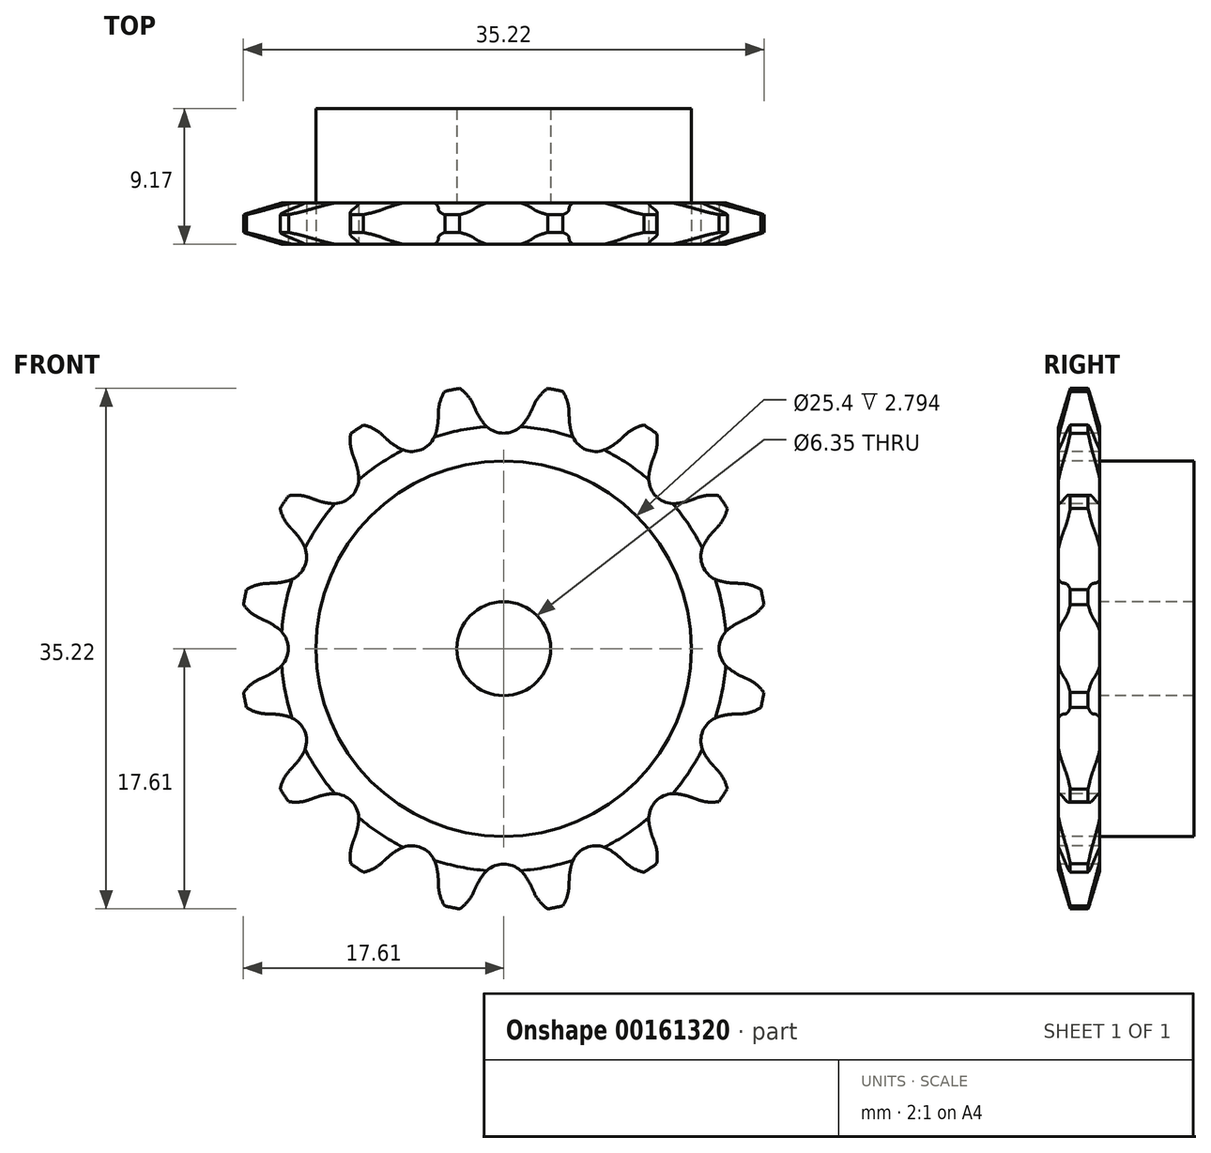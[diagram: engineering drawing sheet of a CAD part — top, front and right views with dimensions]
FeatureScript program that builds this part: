
annotation { "Feature Type Name" : "Feature", "Feature Type Description" : "" }
export const myFeature = defineFeature(function(context is Context, id is Id, definition is map)
    precondition{}
    {
        {
            var Q0;
            Q0=qCreatedBy(makeId("Right.planeOp"),FACE);
            var sketch = newSketch(context, id + "F0", { "sketchPlane" : qUnion([Q0])});
            skLineSegment(sketch, "E0", {"start": v(0, 0) * mm, "end": v(11.72, 0) * mm, "construction": true});
            skLineSegment(sketch, "E1.bottom", {"start": v(0, 3.18) * mm, "end": v(2.8, 3.18) * mm});
            skLineSegment(sketch, "E1.top", {"start": v(0, 17.86) * mm, "end": v(2.8, 17.86) * mm});
            skLineSegment(sketch, "E1.left", {"start": v(0, 3.18) * mm, "end": v(0, 17.86) * mm});
            skLineSegment(sketch, "E1.right", {"start": v(2.8, 3.18) * mm, "end": v(2.8, 17.86) * mm});
            skLineSegment(sketch, "E2.bottom", {"start": v(0, 3.18) * mm, "end": v(9.17, 3.18) * mm});
            skLineSegment(sketch, "E2.top", {"start": v(0, 12.7) * mm, "end": v(9.17, 12.7) * mm});
            skLineSegment(sketch, "E2.left", {"start": v(0, 3.18) * mm, "end": v(0, 12.7) * mm});
            skLineSegment(sketch, "E2.right", {"start": v(9.17, 3.18) * mm, "end": v(9.17, 12.7) * mm});
            skLineSegment(sketch, "E3.MirrorCS", {"start": v(0, -17.86) * mm, "end": v(2.8, -17.86) * mm});
            skLineSegment(sketch, "E4.MirrorCS", {"start": v(0, -3.18) * mm, "end": v(2.8, -3.18) * mm});
            skLineSegment(sketch, "E5.MirrorCS", {"start": v(9.17, -3.18) * mm, "end": v(9.17, -12.7) * mm});
            skLineSegment(sketch, "E6.MirrorCS", {"start": v(0, -3.18) * mm, "end": v(0, -17.86) * mm});
            skLineSegment(sketch, "E7.MirrorCS", {"start": v(2.8, -3.18) * mm, "end": v(2.8, -17.86) * mm});
            skLineSegment(sketch, "E8.MirrorCS", {"start": v(0, -3.18) * mm, "end": v(9.17, -3.18) * mm});
            skLineSegment(sketch, "E9.MirrorCS", {"start": v(0, -12.7) * mm, "end": v(9.17, -12.7) * mm});
            skLineSegment(sketch, "E10.MirrorCS", {"start": v(0, -3.18) * mm, "end": v(0, -12.7) * mm});
            skLineSegment(sketch, "E11.bottom", {"start": v(9.17, 3.18) * mm, "end": v(11.96, 3.18) * mm});
            skLineSegment(sketch, "E11.top", {"start": v(9.17, 17.86) * mm, "end": v(11.96, 17.86) * mm});
            skLineSegment(sketch, "E11.left", {"start": v(9.17, 3.18) * mm, "end": v(9.17, 17.86) * mm});
            skLineSegment(sketch, "E11.right", {"start": v(11.96, 3.18) * mm, "end": v(11.96, 17.86) * mm});
            skLineSegment(sketch, "E12.MirrorCS", {"start": v(9.17, -3.18) * mm, "end": v(9.17, -17.86) * mm});
            skLineSegment(sketch, "E13.MirrorCS", {"start": v(9.17, -17.86) * mm, "end": v(11.96, -17.86) * mm});
            skLineSegment(sketch, "E14.MirrorCS", {"start": v(11.96, -3.18) * mm, "end": v(11.96, -17.86) * mm});
            skLineSegment(sketch, "E15.MirrorCS", {"start": v(9.17, -3.18) * mm, "end": v(11.96, -3.18) * mm});
            skSolve(sketch);
        }
        {
            var Q0;
            {var subQ5=sQuery(id+"F0.wireOp",EDGE,"E2.right");Q0=makeQuery(id+"F0.imprint","IMPRINT",FACE,{"disambiguationData":[TD([[makeQuery(id+"F0.imprint","IMPRINT",EDGE,{"derivedFrom":subQ5}),1.0]])]});}
            var Q1;
            {var subQ5=sQuery(id+"F0.wireOp",EDGE,"E2.left");Q1=makeQuery(id+"F0.imprint","IMPRINT",FACE,{"disambiguationData":[TD([[makeQuery(id+"F0.imprint","IMPRINT",EDGE,{"derivedFrom":subQ5}),-1.0]])]});}
            var Q2;
            {var subQ0=sQuery(id+"F0.wireOp",EDGE,"E1.top");Q2=makeQuery(id+"F0.imprint","IMPRINT",FACE,{"disambiguationData":[TD([[makeQuery(id+"F0.imprint","IMPRINT",EDGE,{"derivedFrom":subQ0}),-1.0]])]});}
            var Q3;
            Q3=sQuery(id+"F0.wireOp",EDGE,"E0");
            revolve(context, id + "F1", {"entities" : qUnion([Q0, Q1, Q2]), "axis" : qUnion([Q3]), "revolveType" : RevolveType.FULL});
        }
        {
            var Q0;
            Q0=makeQuery(id+"F1.opRevolve","SWEPT_EDGE",EDGE,{"disambiguationData":[OSD([sQuery(id+"F0.wireOp",EDGE,"E1.top"),sQuery(id+"F0.wireOp",EDGE,"E1.left")])]});
            var Q1;
            Q1=makeQuery(id+"F1.opRevolve","SWEPT_EDGE",EDGE,{"disambiguationData":[OSD([sQuery(id+"F0.wireOp",EDGE,"E1.top"),sQuery(id+"F0.wireOp",EDGE,"E1.right")])]});
            chamfer(context, id + "F2", {"entities" : qUnion([Q0, Q1]), "chamferType" : ChamferType.TWO_OFFSETS, "width1" : 2.8 * mm, "oppositeDirection" : false, "width2" : 0.8 * mm, "tangentPropagation" : true});
        }
        {
            var Q0;
            Q0=makeQuery(id+"F1.opRevolve","SWEPT_FACE",FACE,{"disambiguationData":[OSD([sQuery(id+"F0.wireOp",EDGE,"E1.left"),sQuery(id+"F0.wireOp",EDGE,"E2.left")])]});
            var sketch = newSketch(context, id + "F3", { "sketchPlane" : qUnion([Q0])});
            skCircle(sketch, "E16", {"center": v(0, 0) * mm, "radius": 16.28 * mm, "construction": true});
            skLineSegment(sketch, "E17", {"start": v(0, 0) * mm, "end": v(0, 16.28) * mm, "construction": true});
            skLineSegment(sketch, "E18", {"start": v(0, 16.28) * mm, "end": v(74.18, 16.28) * mm, "construction": true});
            skLineSegment(sketch, "E19", {"start": v(0, 16.28) * mm, "end": v(2.06, 17.93) * mm, "construction": true});
            skLineSegment(sketch, "E20", {"start": v(2.06, 17.93) * mm, "end": v(-1.9, 16.15) * mm, "construction": true});
            skLineSegment(sketch, "E21", {"start": v(-1.9, 16.15) * mm, "end": v(-2.05, 16.5) * mm});
            skLineSegment(sketch, "E22", {"start": v(0, 0) * mm, "end": v(-3.56, 17.92) * mm, "construction": true});
            skArc(sketch, "E23", {"start": v(-3.56, 17.92) * mm, "mid": v(-6.4, 13.4) * mm, "end": v(-2.05, 16.5) * mm, "construction": true});
            skArc(sketch, "E24", {"start": v(-2.05, 16.5) * mm, "mid": v(-2.67, 17.35) * mm, "end": v(-3.56, 17.92) * mm});
            skLineSegment(sketch, "E25", {"start": v(7.6, -4.93) * mm, "end": v(-1.9, 16.16) * mm, "construction": true});
            skArc(sketch, "E26", {"start": v(-1.9, 16.15) * mm, "mid": v(-1.64, 15.66) * mm, "end": v(-1.32, 15.21) * mm});
            skArc(sketch, "E27", {"start": v(-1.32, 15.21) * mm, "mid": v(5.76, 20.2) * mm, "end": v(-1.9, 16.15) * mm, "construction": true});
            skArc(sketch, "E28.0.MirrorCS", {"start": v(1.9, 16.15) * mm, "mid": v(1.64, 15.66) * mm, "end": v(1.32, 15.21) * mm});
            skLineSegment(sketch, "E29.0.MirrorCS", {"start": v(1.9, 16.15) * mm, "end": v(2.05, 16.5) * mm});
            skArc(sketch, "E30.0.MirrorCS", {"start": v(2.05, 16.5) * mm, "mid": v(2.67, 17.35) * mm, "end": v(3.56, 17.92) * mm});
            skArc(sketch, "E31", {"start": v(-1.32, 15.21) * mm, "mid": v(0, 14.58) * mm, "end": v(1.32, 15.21) * mm});
            skArc(sketch, "E32", {"start": v(1.32, 15.21) * mm, "mid": v(0, 17.97) * mm, "end": v(-1.32, 15.21) * mm, "construction": true});
            skArc(sketch, "E33.1.0", {"start": v(-7.93, 14.2) * mm, "mid": v(-7.5, 13.84) * mm, "end": v(-7.04, 13.55) * mm});
            skArc(sketch, "E33.1.1", {"start": v(-8.2, 14.45) * mm, "mid": v(-9.1, 15.01) * mm, "end": v(-10.15, 15.19) * mm});
            skLineSegment(sketch, "E33.1.2", {"start": v(-7.93, 14.2) * mm, "end": v(-8.2, 14.45) * mm});
            skArc(sketch, "E33.1.3", {"start": v(-7.04, 13.55) * mm, "mid": v(-5.58, 13.47) * mm, "end": v(-4.6, 14.56) * mm});
            skArc(sketch, "E33.1.4", {"start": v(-4.43, 15.64) * mm, "mid": v(-4.48, 15.1) * mm, "end": v(-4.6, 14.56) * mm});
            skArc(sketch, "E33.1.5", {"start": v(-4.42, 16.02) * mm, "mid": v(-4.18, 17.05) * mm, "end": v(-3.56, 17.92) * mm});
            skLineSegment(sketch, "E33.1.6", {"start": v(-4.43, 15.64) * mm, "end": v(-4.42, 16.02) * mm});
            skArc(sketch, "E33.2.0", {"start": v(-12.76, 10.08) * mm, "mid": v(-12.23, 9.91) * mm, "end": v(-11.7, 9.82) * mm});
            skArc(sketch, "E33.2.1", {"start": v(-13.11, 10.21) * mm, "mid": v(-14.16, 10.39) * mm, "end": v(-15.19, 10.15) * mm});
            skLineSegment(sketch, "E33.2.2", {"start": v(-12.76, 10.08) * mm, "end": v(-13.11, 10.21) * mm});
            skArc(sketch, "E33.2.3", {"start": v(-11.7, 9.82) * mm, "mid": v(-10.3, 10.3) * mm, "end": v(-9.82, 11.7) * mm});
            skArc(sketch, "E33.2.4", {"start": v(-10.08, 12.76) * mm, "mid": v(-9.91, 12.23) * mm, "end": v(-9.82, 11.7) * mm});
            skArc(sketch, "E33.2.5", {"start": v(-10.21, 13.11) * mm, "mid": v(-10.39, 14.16) * mm, "end": v(-10.15, 15.19) * mm});
            skLineSegment(sketch, "E33.2.6", {"start": v(-10.08, 12.76) * mm, "end": v(-10.21, 13.11) * mm});
            skArc(sketch, "E33.3.0", {"start": v(-15.64, 4.43) * mm, "mid": v(-15.1, 4.48) * mm, "end": v(-14.56, 4.6) * mm});
            skArc(sketch, "E33.3.1", {"start": v(-16.02, 4.42) * mm, "mid": v(-17.05, 4.18) * mm, "end": v(-17.92, 3.56) * mm});
            skLineSegment(sketch, "E33.3.2", {"start": v(-15.64, 4.43) * mm, "end": v(-16.02, 4.42) * mm});
            skArc(sketch, "E33.3.3", {"start": v(-14.56, 4.6) * mm, "mid": v(-13.47, 5.58) * mm, "end": v(-13.55, 7.04) * mm});
            skArc(sketch, "E33.3.4", {"start": v(-14.2, 7.93) * mm, "mid": v(-13.84, 7.5) * mm, "end": v(-13.55, 7.04) * mm});
            skArc(sketch, "E33.3.5", {"start": v(-14.45, 8.2) * mm, "mid": v(-15.01, 9.1) * mm, "end": v(-15.19, 10.15) * mm});
            skLineSegment(sketch, "E33.3.6", {"start": v(-14.2, 7.93) * mm, "end": v(-14.45, 8.2) * mm});
            skArc(sketch, "E33.4.0", {"start": v(-16.15, -1.9) * mm, "mid": v(-15.66, -1.64) * mm, "end": v(-15.21, -1.32) * mm});
            skArc(sketch, "E33.4.1", {"start": v(-16.5, -2.05) * mm, "mid": v(-17.35, -2.67) * mm, "end": v(-17.92, -3.56) * mm});
            skLineSegment(sketch, "E33.4.2", {"start": v(-16.15, -1.9) * mm, "end": v(-16.5, -2.05) * mm});
            skArc(sketch, "E33.4.3", {"start": v(-15.21, -1.32) * mm, "mid": v(-14.58, 0) * mm, "end": v(-15.21, 1.32) * mm});
            skArc(sketch, "E33.4.4", {"start": v(-16.15, 1.9) * mm, "mid": v(-15.66, 1.64) * mm, "end": v(-15.21, 1.32) * mm});
            skArc(sketch, "E33.4.5", {"start": v(-16.5, 2.05) * mm, "mid": v(-17.35, 2.67) * mm, "end": v(-17.92, 3.56) * mm});
            skLineSegment(sketch, "E33.4.6", {"start": v(-16.15, 1.9) * mm, "end": v(-16.5, 2.05) * mm});
            skArc(sketch, "E33.5.0", {"start": v(-14.2, -7.93) * mm, "mid": v(-13.84, -7.5) * mm, "end": v(-13.55, -7.04) * mm});
            skArc(sketch, "E33.5.1", {"start": v(-14.45, -8.2) * mm, "mid": v(-15.01, -9.1) * mm, "end": v(-15.19, -10.15) * mm});
            skLineSegment(sketch, "E33.5.2", {"start": v(-14.2, -7.93) * mm, "end": v(-14.45, -8.2) * mm});
            skArc(sketch, "E33.5.3", {"start": v(-13.55, -7.04) * mm, "mid": v(-13.47, -5.58) * mm, "end": v(-14.56, -4.6) * mm});
            skArc(sketch, "E33.5.4", {"start": v(-15.64, -4.43) * mm, "mid": v(-15.1, -4.48) * mm, "end": v(-14.56, -4.6) * mm});
            skArc(sketch, "E33.5.5", {"start": v(-16.02, -4.42) * mm, "mid": v(-17.05, -4.18) * mm, "end": v(-17.92, -3.56) * mm});
            skLineSegment(sketch, "E33.5.6", {"start": v(-15.64, -4.43) * mm, "end": v(-16.02, -4.42) * mm});
            skArc(sketch, "E33.6.0", {"start": v(-10.08, -12.76) * mm, "mid": v(-9.91, -12.23) * mm, "end": v(-9.82, -11.7) * mm});
            skArc(sketch, "E33.6.1", {"start": v(-10.21, -13.11) * mm, "mid": v(-10.39, -14.16) * mm, "end": v(-10.15, -15.19) * mm});
            skLineSegment(sketch, "E33.6.2", {"start": v(-10.08, -12.76) * mm, "end": v(-10.21, -13.11) * mm});
            skArc(sketch, "E33.6.3", {"start": v(-9.82, -11.7) * mm, "mid": v(-10.3, -10.3) * mm, "end": v(-11.7, -9.82) * mm});
            skArc(sketch, "E33.6.4", {"start": v(-12.76, -10.08) * mm, "mid": v(-12.23, -9.91) * mm, "end": v(-11.7, -9.82) * mm});
            skArc(sketch, "E33.6.5", {"start": v(-13.11, -10.21) * mm, "mid": v(-14.16, -10.39) * mm, "end": v(-15.19, -10.15) * mm});
            skLineSegment(sketch, "E33.6.6", {"start": v(-12.76, -10.08) * mm, "end": v(-13.11, -10.21) * mm});
            skArc(sketch, "E33.7.0", {"start": v(-4.43, -15.64) * mm, "mid": v(-4.48, -15.1) * mm, "end": v(-4.6, -14.56) * mm});
            skArc(sketch, "E33.7.1", {"start": v(-4.42, -16.02) * mm, "mid": v(-4.18, -17.05) * mm, "end": v(-3.56, -17.92) * mm});
            skLineSegment(sketch, "E33.7.2", {"start": v(-4.43, -15.64) * mm, "end": v(-4.42, -16.02) * mm});
            skArc(sketch, "E33.7.3", {"start": v(-4.6, -14.56) * mm, "mid": v(-5.58, -13.47) * mm, "end": v(-7.04, -13.55) * mm});
            skArc(sketch, "E33.7.4", {"start": v(-7.93, -14.2) * mm, "mid": v(-7.5, -13.84) * mm, "end": v(-7.04, -13.55) * mm});
            skArc(sketch, "E33.7.5", {"start": v(-8.2, -14.45) * mm, "mid": v(-9.1, -15.01) * mm, "end": v(-10.15, -15.19) * mm});
            skLineSegment(sketch, "E33.7.6", {"start": v(-7.93, -14.2) * mm, "end": v(-8.2, -14.45) * mm});
            skArc(sketch, "E33.8.0", {"start": v(1.9, -16.15) * mm, "mid": v(1.64, -15.66) * mm, "end": v(1.32, -15.21) * mm});
            skArc(sketch, "E33.8.1", {"start": v(2.05, -16.5) * mm, "mid": v(2.67, -17.35) * mm, "end": v(3.56, -17.92) * mm});
            skLineSegment(sketch, "E33.8.2", {"start": v(1.9, -16.15) * mm, "end": v(2.05, -16.5) * mm});
            skArc(sketch, "E33.8.3", {"start": v(1.32, -15.21) * mm, "mid": v(0, -14.58) * mm, "end": v(-1.32, -15.21) * mm});
            skArc(sketch, "E33.8.4", {"start": v(-1.9, -16.15) * mm, "mid": v(-1.64, -15.66) * mm, "end": v(-1.32, -15.21) * mm});
            skArc(sketch, "E33.8.5", {"start": v(-2.05, -16.5) * mm, "mid": v(-2.67, -17.35) * mm, "end": v(-3.56, -17.92) * mm});
            skLineSegment(sketch, "E33.8.6", {"start": v(-1.9, -16.15) * mm, "end": v(-2.05, -16.5) * mm});
            skArc(sketch, "E33.9.0", {"start": v(7.93, -14.2) * mm, "mid": v(7.5, -13.84) * mm, "end": v(7.04, -13.55) * mm});
            skArc(sketch, "E33.9.1", {"start": v(8.2, -14.45) * mm, "mid": v(9.1, -15.01) * mm, "end": v(10.15, -15.19) * mm});
            skLineSegment(sketch, "E33.9.2", {"start": v(7.93, -14.2) * mm, "end": v(8.2, -14.45) * mm});
            skArc(sketch, "E33.9.3", {"start": v(7.04, -13.55) * mm, "mid": v(5.58, -13.47) * mm, "end": v(4.6, -14.56) * mm});
            skArc(sketch, "E33.9.4", {"start": v(4.43, -15.64) * mm, "mid": v(4.48, -15.1) * mm, "end": v(4.6, -14.56) * mm});
            skArc(sketch, "E33.9.5", {"start": v(4.42, -16.02) * mm, "mid": v(4.18, -17.05) * mm, "end": v(3.56, -17.92) * mm});
            skLineSegment(sketch, "E33.9.6", {"start": v(4.43, -15.64) * mm, "end": v(4.42, -16.02) * mm});
            skArc(sketch, "E33.10.0", {"start": v(12.76, -10.08) * mm, "mid": v(12.23, -9.91) * mm, "end": v(11.7, -9.82) * mm});
            skArc(sketch, "E33.10.1", {"start": v(13.11, -10.21) * mm, "mid": v(14.16, -10.39) * mm, "end": v(15.19, -10.15) * mm});
            skLineSegment(sketch, "E33.10.2", {"start": v(12.76, -10.08) * mm, "end": v(13.11, -10.21) * mm});
            skArc(sketch, "E33.10.3", {"start": v(11.7, -9.82) * mm, "mid": v(10.3, -10.3) * mm, "end": v(9.82, -11.7) * mm});
            skArc(sketch, "E33.10.4", {"start": v(10.08, -12.76) * mm, "mid": v(9.91, -12.23) * mm, "end": v(9.82, -11.7) * mm});
            skArc(sketch, "E33.10.5", {"start": v(10.21, -13.11) * mm, "mid": v(10.39, -14.16) * mm, "end": v(10.15, -15.19) * mm});
            skLineSegment(sketch, "E33.10.6", {"start": v(10.08, -12.76) * mm, "end": v(10.21, -13.11) * mm});
            skArc(sketch, "E33.11.0", {"start": v(15.64, -4.43) * mm, "mid": v(15.1, -4.48) * mm, "end": v(14.56, -4.6) * mm});
            skArc(sketch, "E33.11.1", {"start": v(16.02, -4.42) * mm, "mid": v(17.05, -4.18) * mm, "end": v(17.92, -3.56) * mm});
            skLineSegment(sketch, "E33.11.2", {"start": v(15.64, -4.43) * mm, "end": v(16.02, -4.42) * mm});
            skArc(sketch, "E33.11.3", {"start": v(14.56, -4.6) * mm, "mid": v(13.47, -5.58) * mm, "end": v(13.55, -7.04) * mm});
            skArc(sketch, "E33.11.4", {"start": v(14.2, -7.93) * mm, "mid": v(13.84, -7.5) * mm, "end": v(13.55, -7.04) * mm});
            skArc(sketch, "E33.11.5", {"start": v(14.45, -8.2) * mm, "mid": v(15.01, -9.1) * mm, "end": v(15.19, -10.15) * mm});
            skLineSegment(sketch, "E33.11.6", {"start": v(14.2, -7.93) * mm, "end": v(14.45, -8.2) * mm});
            skArc(sketch, "E33.12.0", {"start": v(16.15, 1.9) * mm, "mid": v(15.66, 1.64) * mm, "end": v(15.21, 1.32) * mm});
            skArc(sketch, "E33.12.1", {"start": v(16.5, 2.05) * mm, "mid": v(17.35, 2.67) * mm, "end": v(17.92, 3.56) * mm});
            skLineSegment(sketch, "E33.12.2", {"start": v(16.15, 1.9) * mm, "end": v(16.5, 2.05) * mm});
            skArc(sketch, "E33.12.3", {"start": v(15.21, 1.32) * mm, "mid": v(14.58, 0) * mm, "end": v(15.21, -1.32) * mm});
            skArc(sketch, "E33.12.4", {"start": v(16.15, -1.9) * mm, "mid": v(15.66, -1.64) * mm, "end": v(15.21, -1.32) * mm});
            skArc(sketch, "E33.12.5", {"start": v(16.5, -2.05) * mm, "mid": v(17.35, -2.67) * mm, "end": v(17.92, -3.56) * mm});
            skLineSegment(sketch, "E33.12.6", {"start": v(16.15, -1.9) * mm, "end": v(16.5, -2.05) * mm});
            skArc(sketch, "E33.13.0", {"start": v(14.2, 7.93) * mm, "mid": v(13.84, 7.5) * mm, "end": v(13.55, 7.04) * mm});
            skArc(sketch, "E33.13.1", {"start": v(14.45, 8.2) * mm, "mid": v(15.01, 9.1) * mm, "end": v(15.19, 10.15) * mm});
            skLineSegment(sketch, "E33.13.2", {"start": v(14.2, 7.93) * mm, "end": v(14.45, 8.2) * mm});
            skArc(sketch, "E33.13.3", {"start": v(13.55, 7.04) * mm, "mid": v(13.47, 5.58) * mm, "end": v(14.56, 4.6) * mm});
            skArc(sketch, "E33.13.4", {"start": v(15.64, 4.43) * mm, "mid": v(15.1, 4.48) * mm, "end": v(14.56, 4.6) * mm});
            skArc(sketch, "E33.13.5", {"start": v(16.02, 4.42) * mm, "mid": v(17.05, 4.18) * mm, "end": v(17.92, 3.56) * mm});
            skLineSegment(sketch, "E33.13.6", {"start": v(15.64, 4.43) * mm, "end": v(16.02, 4.42) * mm});
            skArc(sketch, "E33.14.0", {"start": v(10.08, 12.76) * mm, "mid": v(9.91, 12.23) * mm, "end": v(9.82, 11.7) * mm});
            skArc(sketch, "E33.14.1", {"start": v(10.21, 13.11) * mm, "mid": v(10.39, 14.16) * mm, "end": v(10.15, 15.19) * mm});
            skLineSegment(sketch, "E33.14.2", {"start": v(10.08, 12.76) * mm, "end": v(10.21, 13.11) * mm});
            skArc(sketch, "E33.14.3", {"start": v(9.82, 11.7) * mm, "mid": v(10.3, 10.3) * mm, "end": v(11.7, 9.82) * mm});
            skArc(sketch, "E33.14.4", {"start": v(12.76, 10.08) * mm, "mid": v(12.23, 9.91) * mm, "end": v(11.7, 9.82) * mm});
            skArc(sketch, "E33.14.5", {"start": v(13.11, 10.21) * mm, "mid": v(14.16, 10.39) * mm, "end": v(15.19, 10.15) * mm});
            skLineSegment(sketch, "E33.14.6", {"start": v(12.76, 10.08) * mm, "end": v(13.11, 10.21) * mm});
            skArc(sketch, "E33.15.0", {"start": v(4.43, 15.64) * mm, "mid": v(4.48, 15.1) * mm, "end": v(4.6, 14.56) * mm});
            skArc(sketch, "E33.15.1", {"start": v(4.42, 16.02) * mm, "mid": v(4.18, 17.05) * mm, "end": v(3.56, 17.92) * mm});
            skLineSegment(sketch, "E33.15.2", {"start": v(4.43, 15.64) * mm, "end": v(4.42, 16.02) * mm});
            skArc(sketch, "E33.15.3", {"start": v(4.6, 14.56) * mm, "mid": v(5.58, 13.47) * mm, "end": v(7.04, 13.55) * mm});
            skArc(sketch, "E33.15.4", {"start": v(7.93, 14.2) * mm, "mid": v(7.5, 13.84) * mm, "end": v(7.04, 13.55) * mm});
            skArc(sketch, "E33.15.5", {"start": v(8.2, 14.45) * mm, "mid": v(9.1, 15.01) * mm, "end": v(10.15, 15.19) * mm});
            skLineSegment(sketch, "E33.15.6", {"start": v(7.93, 14.2) * mm, "end": v(8.2, 14.45) * mm});
            skSolve(sketch);
        }
        {
            var Q0;
            Q0=qSketchRegion(id+"F3",true);
            extrude(context, id + "F4", {"entities" : qUnion([Q0]), "operationType" : NewBodyOperationType.INTERSECT, "endBound" : BoundingType.THROUGH_ALL, "oppositeDirection" : true, "depth" : 25.4 * mm});
        }
    });
